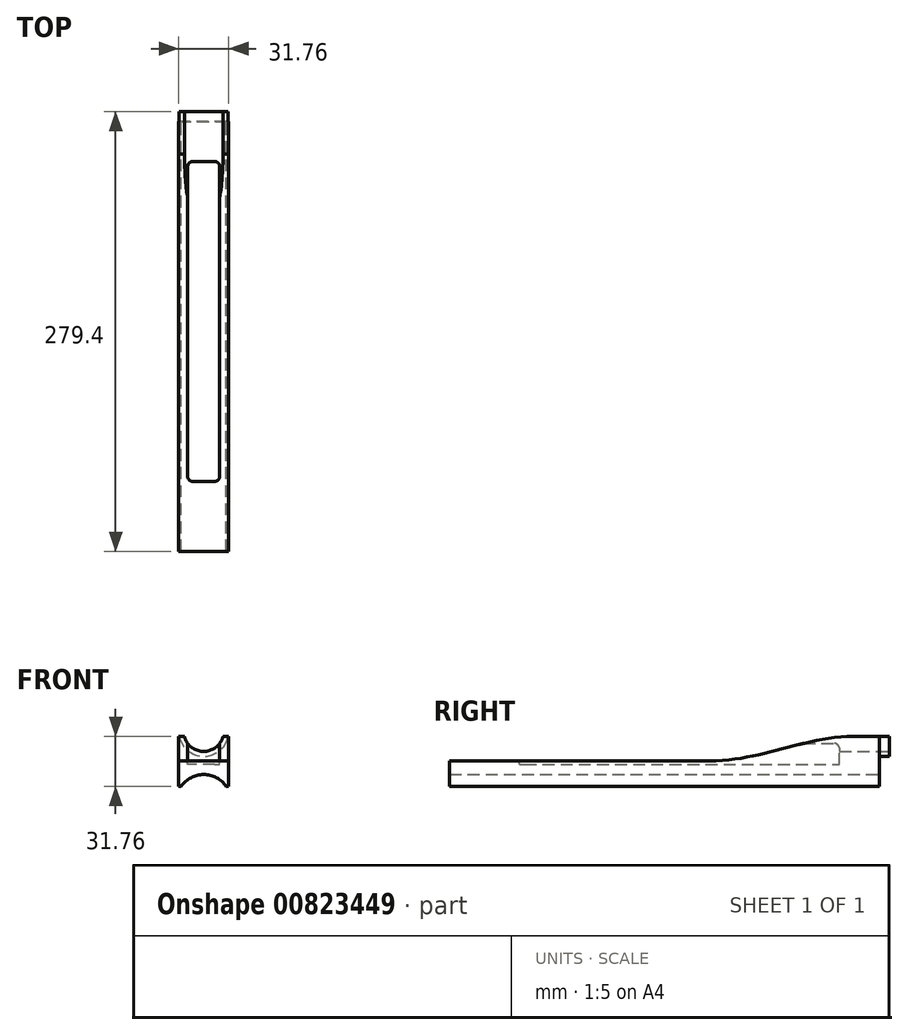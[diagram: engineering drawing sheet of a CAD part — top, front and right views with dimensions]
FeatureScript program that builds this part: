
annotation { "Feature Type Name" : "Feature", "Feature Type Description" : "" }
export const myFeature = defineFeature(function(context is Context, id is Id, definition is map)
    precondition{}
    {
        {
            var Q0;
            Q0=qCreatedBy(makeId("Front.planeOp"),FACE);
            var sketch = newSketch(context, id + "F0", { "sketchPlane" : qUnion([Q0])});
            skCircle(sketch, "E0", {"center": v(0, 0) * mm, "radius": 12.7 * mm});
            skCircle(sketch, "E1", {"center": v(0, 0) * mm, "radius": 15.88 * mm});
            skCircle(sketch, "E2", {"center": v(0, 0) * mm, "radius": 26.67 * mm});
            skLineSegment(sketch, "E3", {"start": v(0, -3.17) * mm, "end": v(0, -27.43) * mm});
            skLineSegment(sketch, "E4", {"start": v(-15.88, -3.17) * mm, "end": v(15.88, -3.17) * mm});
            skLineSegment(sketch, "E5", {"start": v(15.87, -3.17) * mm, "end": v(15.88, -34.92) * mm});
            skLineSegment(sketch, "E6", {"start": v(15.88, -34.92) * mm, "end": v(-15.88, -34.92) * mm});
            skLineSegment(sketch, "E7", {"start": v(-15.87, -34.92) * mm, "end": v(-15.88, -3.17) * mm});
            skArc(sketch, "E8", {"start": v(14.34, -34.93) * mm, "mid": v(0, -27.43) * mm, "end": v(-14.34, -34.92) * mm});
            skCircle(sketch, "E9", {"center": v(0, 0) * mm, "radius": 30.48 * mm});
            skSolve(sketch);
        }
        {
            var Q0;
            {var subQ0=sQuery(id+"F0.wireOp",EDGE,"E3");var subQ1=sQuery(id+"F0.wireOp",EDGE,"E1");var subQ2=makeQuery(id+"F0.imprint","INTERSECT",VERTEX,{"derivedFrom":[subQ1,subQ0]});Q0=makeQuery(id+"F0.imprint","IMPRINT",FACE,{"disambiguationData":[TD([[makeQuery(id+"F0.imprint","IMPRINT",EDGE,{"disambiguationData":[TD([[subQ2,1.0]])],"derivedFrom":subQ1}),-1.0]])]});}
            var Q1;
            {var subQ3=sQuery(id+"F0.wireOp",EDGE,"E1");var subQ5=sQuery(id+"F0.wireOp",EDGE,"E3");var subQ9=makeQuery(id+"F0.imprint","INTERSECT",VERTEX,{"derivedFrom":[subQ3,subQ5]});Q1=makeQuery(id+"F0.imprint","IMPRINT",FACE,{"disambiguationData":[TD([[makeQuery(id+"F0.imprint","IMPRINT",EDGE,{"disambiguationData":[TD([[subQ9,-1.0]])],"derivedFrom":subQ3}),-1.0]])]});}
            var Q2;
            {var subQ1=sQuery(id+"F0.wireOp",EDGE,"E3");var subQ5=sQuery(id+"F0.wireOp",EDGE,"E2");var subQ6=makeQuery(id+"F0.imprint","INTERSECT",VERTEX,{"derivedFrom":[subQ5,subQ1]});Q2=makeQuery(id+"F0.imprint","IMPRINT",FACE,{"disambiguationData":[TD([[makeQuery(id+"F0.imprint","IMPRINT",EDGE,{"disambiguationData":[TD([[subQ6,1.0]])],"derivedFrom":subQ5}),-1.0]])]});}
            var Q3;
            {var subQ0=sQuery(id+"F0.wireOp",EDGE,"E7");var subQ1=sQuery(id+"F0.wireOp",EDGE,"E6");var subQ2=makeQuery(id+"F0.imprint","INTERSECT",VERTEX,{"derivedFrom":[subQ1,subQ0]});Q3=makeQuery(id+"F0.imprint","IMPRINT",FACE,{"disambiguationData":[TD([[makeQuery(id+"F0.imprint","IMPRINT",EDGE,{"disambiguationData":[TD([[subQ2,1.0]])],"derivedFrom":subQ1}),-1.0]])]});}
            var Q4;
            {var subQ1=sQuery(id+"F0.wireOp",EDGE,"E3");var subQ5=sQuery(id+"F0.wireOp",EDGE,"E2");var subQ6=makeQuery(id+"F0.imprint","INTERSECT",VERTEX,{"derivedFrom":[subQ5,subQ1]});Q4=makeQuery(id+"F0.imprint","IMPRINT",FACE,{"disambiguationData":[TD([[makeQuery(id+"F0.imprint","IMPRINT",EDGE,{"disambiguationData":[TD([[subQ6,-1.0]])],"derivedFrom":subQ5}),-1.0]])]});}
            var Q5;
            {var subQ0=sQuery(id+"F0.wireOp",EDGE,"E6");var subQ1=sQuery(id+"F0.wireOp",EDGE,"E5");var subQ2=makeQuery(id+"F0.imprint","INTERSECT",VERTEX,{"derivedFrom":[subQ1,subQ0]});Q5=makeQuery(id+"F0.imprint","IMPRINT",FACE,{"disambiguationData":[TD([[makeQuery(id+"F0.imprint","IMPRINT",EDGE,{"disambiguationData":[TD([[subQ2,1.0]])],"derivedFrom":subQ1}),-1.0]])]});}
            var Q6;
            {var subQ0=sQuery(id+"F0.wireOp",EDGE,"E3");var subQ1=sQuery(id+"F0.wireOp",EDGE,"E0");var subQ2=makeQuery(id+"F0.imprint","INTERSECT",VERTEX,{"derivedFrom":[subQ1,subQ0]});Q6=makeQuery(id+"F0.imprint","IMPRINT",FACE,{"disambiguationData":[TD([[makeQuery(id+"F0.imprint","IMPRINT",EDGE,{"disambiguationData":[TD([[subQ2,-1.0]])],"derivedFrom":subQ1}),-1.0]])]});}
            var Q7;
            {var subQ0=sQuery(id+"F0.wireOp",EDGE,"E3");var subQ1=sQuery(id+"F0.wireOp",EDGE,"E0");var subQ2=makeQuery(id+"F0.imprint","INTERSECT",VERTEX,{"derivedFrom":[subQ1,subQ0]});Q7=makeQuery(id+"F0.imprint","IMPRINT",FACE,{"disambiguationData":[TD([[makeQuery(id+"F0.imprint","IMPRINT",EDGE,{"disambiguationData":[TD([[subQ2,1.0]])],"derivedFrom":subQ1}),-1.0]])]});}
            extrude(context, id + "F1", {"entities" : qUnion([Q0, Q1, Q2, Q3, Q4, Q5, Q6, Q7]), "depth" : 273.05 * mm, "offsetDistance" : 25.4 * mm});
        }
        {
            var Q0;
            {var subQ0=sQuery(id+"F0.wireOp",EDGE,"E3");var subQ1=sQuery(id+"F0.wireOp",EDGE,"E0");var subQ2=makeQuery(id+"F0.imprint","INTERSECT",VERTEX,{"derivedFrom":[subQ1,subQ0]});Q0=makeQuery(id+"F0.imprint","IMPRINT",FACE,{"disambiguationData":[TD([[makeQuery(id+"F0.imprint","IMPRINT",EDGE,{"disambiguationData":[TD([[subQ2,-1.0]])],"derivedFrom":subQ1}),-1.0]])]});}
            var Q1;
            {var subQ0=sQuery(id+"F0.wireOp",EDGE,"E3");var subQ1=sQuery(id+"F0.wireOp",EDGE,"E0");var subQ2=makeQuery(id+"F0.imprint","INTERSECT",VERTEX,{"derivedFrom":[subQ1,subQ0]});Q1=makeQuery(id+"F0.imprint","IMPRINT",FACE,{"disambiguationData":[TD([[makeQuery(id+"F0.imprint","IMPRINT",EDGE,{"disambiguationData":[TD([[subQ2,1.0]])],"derivedFrom":subQ1}),-1.0]])]});}
            extrude(context, id + "F2", {"entities" : qUnion([Q0, Q1]), "operationType" : NewBodyOperationType.ADD, "oppositeDirection" : true, "depth" : 6.35 * mm, "offsetDistance" : 25.4 * mm});
        }
        {
            var Q0;
            Q0=qCreatedBy(makeId("Right.planeOp"),FACE);
            var sketch = newSketch(context, id + "F3", { "sketchPlane" : qUnion([Q0])});
            skLineSegment(sketch, "E10", {"start": v(6.41, -3.09) * mm, "end": v(-18.99, -3.09) * mm});
            skLineSegment(sketch, "E11", {"start": v(-285.69, -18.73) * mm, "end": v(-107.89, -18.73) * mm});
            skFitSpline(sketch, "E12", {"points": [v(-18.99, -3.09) * mm, v(-107.89, -18.73) * mm], "startDerivative": vector(-96.53, -4.76) * mm, "endDerivative": vector(-97.3, -0.42) * mm});
            skLineSegment(sketch, "E13", {"start": v(-18.99, -3.09) * mm, "end": v(-285.69, -3.09) * mm});
            skLineSegment(sketch, "E14", {"start": v(-285.69, -3.09) * mm, "end": v(-285.69, -18.73) * mm});
            skSolve(sketch);
        }
        {
            var Q0;
            Q0=makeQuery(id+"F3.imprint","IMPRINT",FACE,{"disambiguationData":[TD([[makeQuery(id+"F3.imprint","IMPRINT",EDGE,{"derivedFrom":sQuery(id+"F3.wireOp",EDGE,"E11")}),1.0]])]});
            extrude(context, id + "F4", {"entities" : qUnion([Q0]), "operationType" : NewBodyOperationType.REMOVE, "endBound" : BoundingType.SYMMETRIC, "oppositeDirection" : true, "depth" : 50.8 * mm, "offsetDistance" : 25.4 * mm});
        }
        {
            var Q0;
            Q0=qCreatedBy(makeId("Top.planeOp"),FACE);
            var sketch = newSketch(context, id + "F5", { "sketchPlane" : qUnion([Q0])});
            skLineSegment(sketch, "E15.bottom", {"start": v(10.16, -228.6) * mm, "end": v(-10.16, -228.6) * mm});
            skLineSegment(sketch, "E15.top", {"start": v(10.16, -25.4) * mm, "end": v(-10.16, -25.4) * mm});
            skLineSegment(sketch, "E15.left", {"start": v(10.16, -228.6) * mm, "end": v(10.16, -25.4) * mm});
            skLineSegment(sketch, "E15.right", {"start": v(-10.16, -228.6) * mm, "end": v(-10.16, -25.4) * mm});
            skPoint(sketch, "E15.middle", {"position": v(0, -127) * mm});
            skSolve(sketch);
        }
        {
            var Q0;
            Q0=makeQuery(id+"F5.imprint","IMPRINT",FACE,{"disambiguationData":[TD([[makeQuery(id+"F5.imprint","IMPRINT",EDGE,{"derivedFrom":sQuery(id+"F5.wireOp",EDGE,"E15.bottom")}),-1.0]])]});
            extrude(context, id + "F6", {"entities" : qUnion([Q0]), "operationType" : NewBodyOperationType.REMOVE, "oppositeDirection" : true, "depth" : 21.08 * mm, "offsetDistance" : 25.4 * mm});
        }
        {
            var Q0;
            Q0=makeQuery(id+"F6.boolean.opBoolean","COPY",EDGE,{"derivedFrom":makeQuery(id+"F6.opExtrude","SWEPT_EDGE",EDGE,{"disambiguationData":[OSD([sQuery(id+"F5.wireOp",EDGE,"E15.top"),sQuery(id+"F5.wireOp",EDGE,"E15.right")])]})});
            var Q1;
            Q1=makeQuery(id+"F6.boolean.opBoolean","COPY",EDGE,{"derivedFrom":makeQuery(id+"F6.opExtrude","SWEPT_EDGE",EDGE,{"disambiguationData":[OSD([sQuery(id+"F5.wireOp",EDGE,"E15.top"),sQuery(id+"F5.wireOp",EDGE,"E15.left")])]})});
            var Q2;
            Q2=makeQuery(id+"F6.boolean.opBoolean","COPY",EDGE,{"derivedFrom":makeQuery(id+"F6.opExtrude","SWEPT_EDGE",EDGE,{"disambiguationData":[OSD([sQuery(id+"F5.wireOp",EDGE,"E15.bottom"),sQuery(id+"F5.wireOp",EDGE,"E15.right")])]})});
            var Q3;
            Q3=makeQuery(id+"F6.boolean.opBoolean","COPY",EDGE,{"derivedFrom":makeQuery(id+"F6.opExtrude","SWEPT_EDGE",EDGE,{"disambiguationData":[OSD([sQuery(id+"F5.wireOp",EDGE,"E15.bottom"),sQuery(id+"F5.wireOp",EDGE,"E15.left")])]})});
            fillet(context, id + "F7", {"entities" : qUnion([Q0, Q1, Q2, Q3]), "tangentPropagation" : true, "radius" : 3.17 * mm, "defaultsChanged" : false, "vertexSettings" : [], "allowEdgeOverflow" : false});
        }
    });
